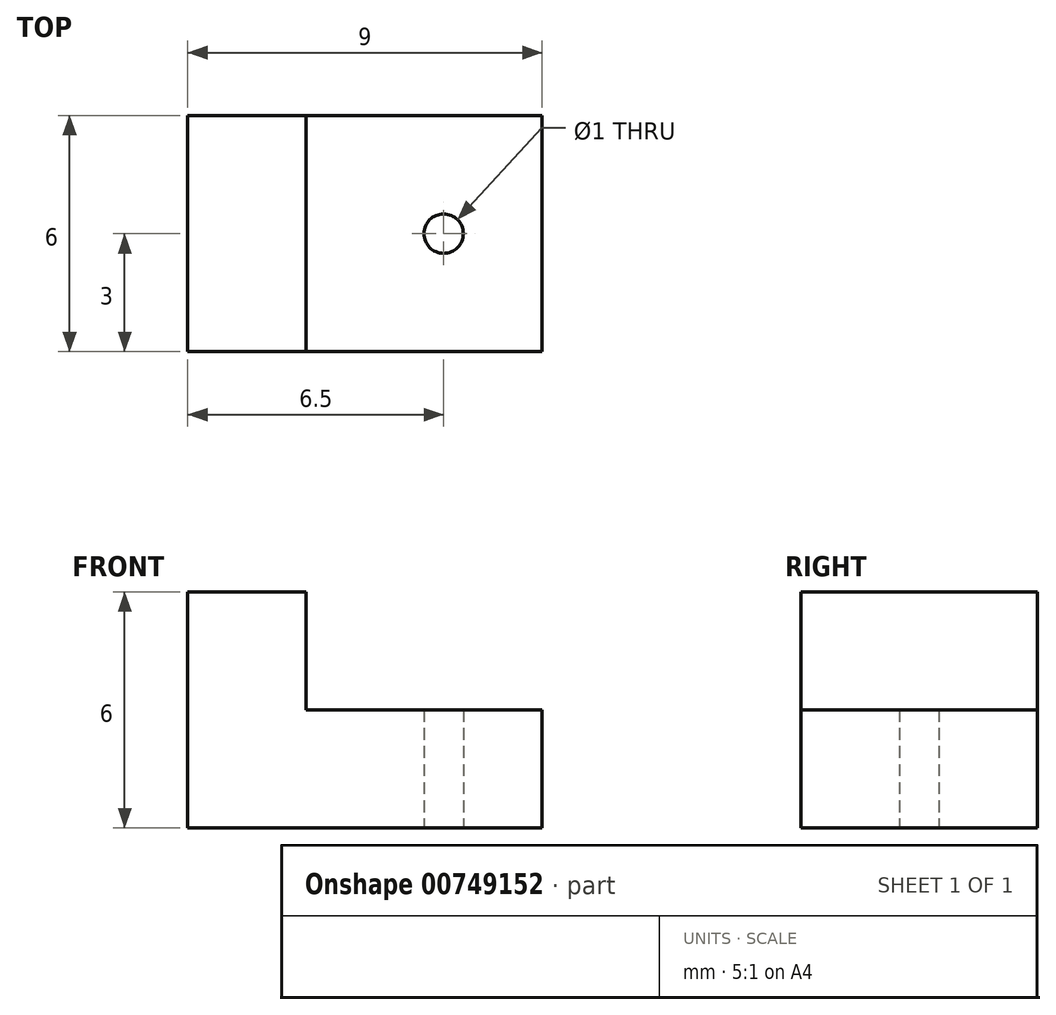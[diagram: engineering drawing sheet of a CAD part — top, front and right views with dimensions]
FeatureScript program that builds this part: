
annotation { "Feature Type Name" : "Feature", "Feature Type Description" : "" }
export const myFeature = defineFeature(function(context is Context, id is Id, definition is map)
    precondition{}
    {
        {
            var Q0;
            Q0=qCreatedBy(makeId("Top.planeOp"),FACE);
            var sketch = newSketch(context, id + "F0", { "sketchPlane" : qUnion([Q0])});
            skLineSegment(sketch, "E0.bottom", {"start": v(-9, 6) * mm, "end": v(-6, 6) * mm});
            skLineSegment(sketch, "E0.top", {"start": v(-9, 0) * mm, "end": v(-6, 0) * mm});
            skLineSegment(sketch, "E0.left", {"start": v(-9, 6) * mm, "end": v(-9, 0) * mm});
            skLineSegment(sketch, "E0.right", {"start": v(-6, 6) * mm, "end": v(-6, 0) * mm});
            skLineSegment(sketch, "E1.bottom", {"start": v(-6, 6) * mm, "end": v(0, 6) * mm});
            skLineSegment(sketch, "E1.top", {"start": v(-6, 0) * mm, "end": v(0, 0) * mm});
            skLineSegment(sketch, "E1.right", {"start": v(0, 6) * mm, "end": v(0, 0) * mm});
            skCircle(sketch, "E2", {"center": v(-2.5, 3) * mm, "radius": 0.5 * mm});
            skSolve(sketch);
        }
        {
            var Q0;
            Q0=makeQuery(id+"F0.imprint","IMPRINT",FACE,{"disambiguationData":[TD([[makeQuery(id+"F0.imprint","IMPRINT",EDGE,{"derivedFrom":sQuery(id+"F0.wireOp",EDGE,"E0.bottom")}),-1.0]])]});
            extrude(context, id + "F1", {"entities" : qUnion([Q0]), "depth" : 6 * mm, "offsetDistance" : 25 * mm});
        }
        {
            var Q0;
            Q0=makeQuery(id+"F0.imprint","IMPRINT",FACE,{"disambiguationData":[TD([[makeQuery(id+"F0.imprint","IMPRINT",EDGE,{"derivedFrom":sQuery(id+"F0.wireOp",EDGE,"E1.bottom")}),-1.0]])]});
            extrude(context, id + "F2", {"entities" : qUnion([Q0]), "operationType" : NewBodyOperationType.ADD, "depth" : 3 * mm, "offsetDistance" : 25 * mm});
        }
    });
